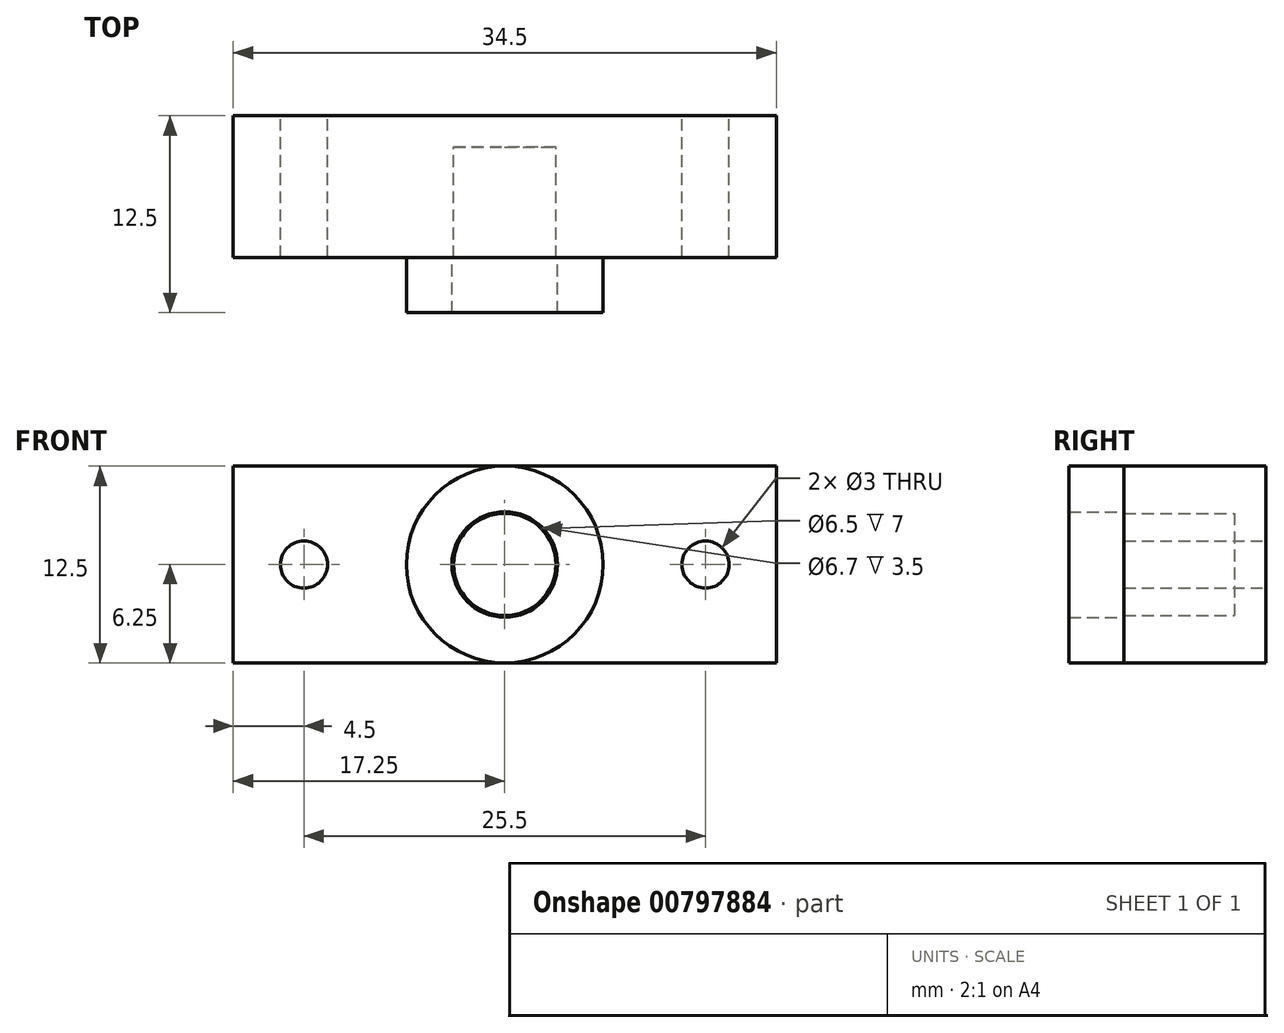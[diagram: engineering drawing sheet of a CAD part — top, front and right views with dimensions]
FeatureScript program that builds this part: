
annotation { "Feature Type Name" : "Feature", "Feature Type Description" : "" }
export const myFeature = defineFeature(function(context is Context, id is Id, definition is map)
    precondition{}
    {
        {
            var Q0;
            Q0=qCreatedBy(makeId("Front.planeOp"),FACE);
            var sketch = newSketch(context, id + "F0", { "sketchPlane" : qUnion([Q0])});
            skCircle(sketch, "E0", {"center": v(0, 0) * mm, "radius": 3.25 * mm});
            skLineSegment(sketch, "E1.bottom", {"start": v(17.25, 6.25) * mm, "end": v(-17.25, 6.25) * mm});
            skLineSegment(sketch, "E1.top", {"start": v(17.25, -6.25) * mm, "end": v(-17.25, -6.25) * mm});
            skLineSegment(sketch, "E1.left", {"start": v(17.25, 6.25) * mm, "end": v(17.25, -6.25) * mm});
            skLineSegment(sketch, "E1.right", {"start": v(-17.25, 6.25) * mm, "end": v(-17.25, -6.25) * mm});
            skCircle(sketch, "E2", {"center": v(12.75, 0) * mm, "radius": 1.5 * mm});
            skCircle(sketch, "E3", {"center": v(-12.75, 0) * mm, "radius": 1.5 * mm});
            skSolve(sketch);
        }
        {
            var Q0;
            Q0 = qSketchRegion(id + "F0", true);
            extrude(context, id + "F1", {"entities" : qUnion([Q0]), "depth" : 9 * mm, "offsetDistance" : 25 * mm});
        }
        {
            var Q0;
            Q0=makeQuery(id+"F1.opExtrude","CAP_FACE",FACE,{"disambiguationData":[OSD([sQuery(id+"F0.wireOp",EDGE,"E0"),sQuery(id+"F0.wireOp",EDGE,"E1.bottom"),sQuery(id+"F0.wireOp",EDGE,"E1.top"),sQuery(id+"F0.wireOp",EDGE,"E1.left"),sQuery(id+"F0.wireOp",EDGE,"E1.right"),sQuery(id+"F0.wireOp",EDGE,"E2"),sQuery(id+"F0.wireOp",EDGE,"E3")])],"isStart":false});
            var sketch = newSketch(context, id + "F2", { "sketchPlane" : qUnion([Q0])});
            skCircle(sketch, "E4", {"center": v(0, 0) * mm, "radius": 3.35 * mm});
            skCircle(sketch, "E5", {"center": v(0, 0) * mm, "radius": 6.25 * mm});
            skSolve(sketch);
        }
        {
            var Q0;
            Q0 = qSketchRegion(id + "F2", true);
            extrude(context, id + "F3", {"entities" : qUnion([Q0]), "operationType" : NewBodyOperationType.ADD, "depth" : 3.5 * mm, "offsetDistance" : 25 * mm});
        }
        {
            var Q0;
            Q0=makeQuery(id+"F1.opExtrude","CAP_FACE",FACE,{"disambiguationData":[OSD([sQuery(id+"F0.wireOp",EDGE,"E0"),sQuery(id+"F0.wireOp",EDGE,"E1.bottom"),sQuery(id+"F0.wireOp",EDGE,"E1.top"),sQuery(id+"F0.wireOp",EDGE,"E1.left"),sQuery(id+"F0.wireOp",EDGE,"E1.right"),sQuery(id+"F0.wireOp",EDGE,"E2"),sQuery(id+"F0.wireOp",EDGE,"E3")])],"isStart":true});
            var sketch = newSketch(context, id + "F4", { "sketchPlane" : qUnion([Q0])});
            skLineSegment(sketch, "E6.bottom", {"start": v(5.48, 4.06) * mm, "end": v(-5.48, 4.06) * mm});
            skLineSegment(sketch, "E6.top", {"start": v(5.48, -4.06) * mm, "end": v(-5.48, -4.06) * mm});
            skLineSegment(sketch, "E6.left", {"start": v(5.48, 4.06) * mm, "end": v(5.48, -4.06) * mm});
            skLineSegment(sketch, "E6.right", {"start": v(-5.48, 4.06) * mm, "end": v(-5.48, -4.06) * mm});
            skPoint(sketch, "E6.middle", {"position": v(0, 0) * mm});
            skSolve(sketch);
        }
        {
            var Q0;
            Q0 = qSketchRegion(id + "F4", true);
            extrude(context, id + "F5", {"entities" : qUnion([Q0]), "operationType" : NewBodyOperationType.ADD, "oppositeDirection" : true, "depth" : 2 * mm, "offsetDistance" : 25 * mm});
        }
    });
